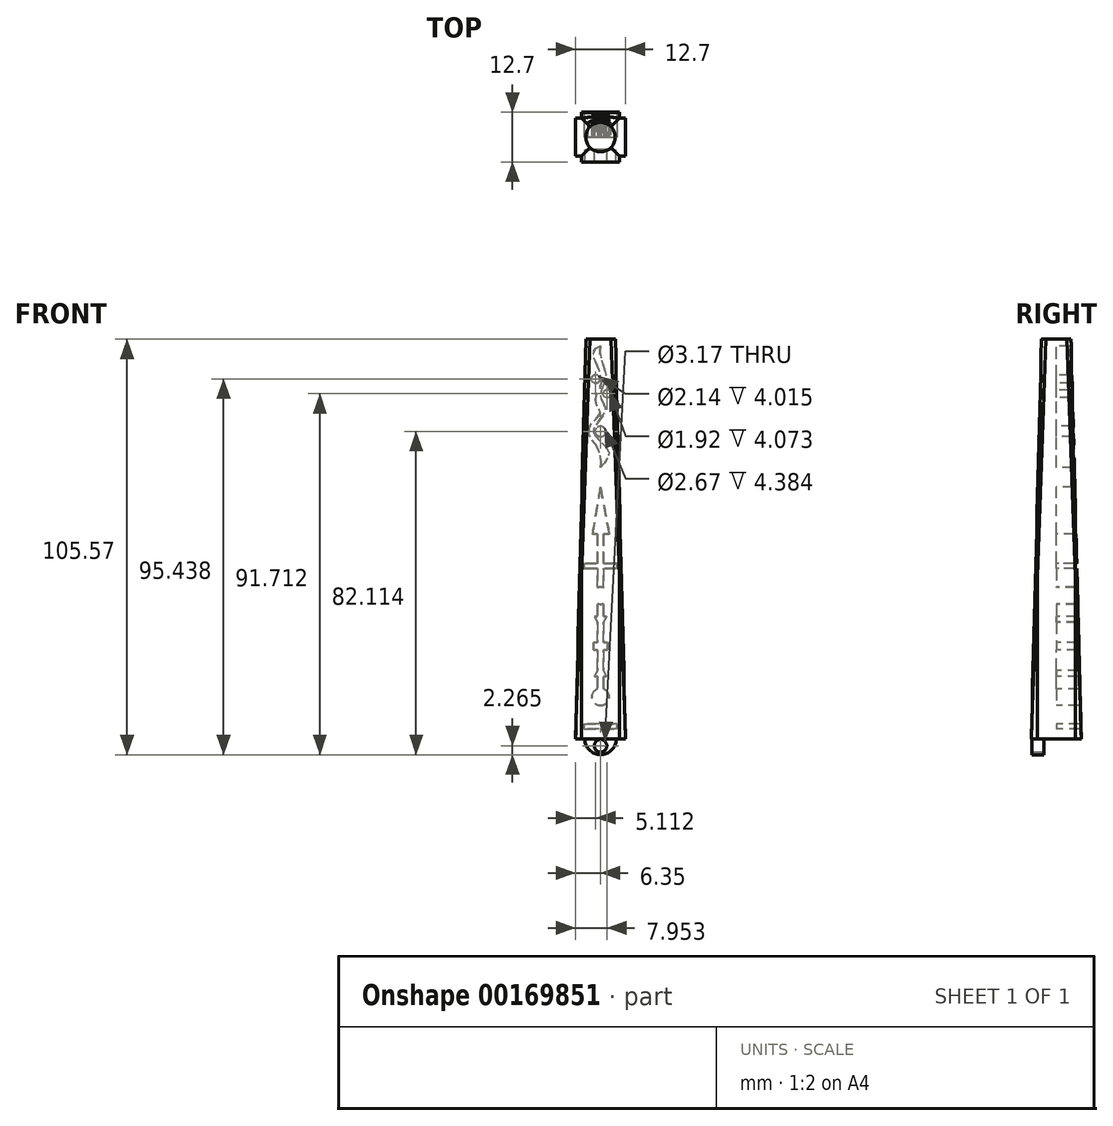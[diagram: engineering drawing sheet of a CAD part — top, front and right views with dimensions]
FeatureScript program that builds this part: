
annotation { "Feature Type Name" : "Feature", "Feature Type Description" : "" }
export const myFeature = defineFeature(function(context is Context, id is Id, definition is map)
    precondition{}
    {
        {
            var Q0;
            Q0=qCreatedBy(makeId("Top.planeOp"),FACE);
            var sketch = newSketch(context, id + "F0", { "sketchPlane" : qUnion([Q0])});
            skLineSegment(sketch, "E0.bottom", {"start": v(6.35, 6.35) * mm, "end": v(-6.35, 6.35) * mm});
            skLineSegment(sketch, "E0.top", {"start": v(6.35, -6.35) * mm, "end": v(-6.35, -6.35) * mm});
            skLineSegment(sketch, "E0.left", {"start": v(6.35, 6.35) * mm, "end": v(6.35, -6.35) * mm});
            skLineSegment(sketch, "E0.right", {"start": v(-6.35, 6.35) * mm, "end": v(-6.35, -6.35) * mm});
            skPoint(sketch, "E0.middle", {"position": v(0, 0) * mm});
            skSolve(sketch);
        }
        {
            var Q0;
            Q0=qCreatedBy(makeId("Top.planeOp"),FACE);
            cPlane(context, id + "F1", {"entities" : qUnion([Q0]), "cplaneType" : CPlaneType.OFFSET, "offset" : 101.6 * mm, "width" : 150 * mm, "height" : 150 * mm});
        }
        {
            var Q0;
            Q0=qCreatedBy(id+"F1.planeOp",FACE);
            var sketch = newSketch(context, id + "F2", { "sketchPlane" : qUnion([Q0])});
            skCircle(sketch, "E1", {"center": v(0, 0) * mm, "radius": 3.75 * mm});
            skSolve(sketch);
        }
        {
            var Q0;
            Q0=makeQuery(id+"F0.imprint","IMPRINT",FACE,{"disambiguationData":[TD([[makeQuery(id+"F0.imprint","IMPRINT",EDGE,{"derivedFrom":sQuery(id+"F0.wireOp",EDGE,"E0.bottom")}),1.0]])]});
            var Q1;
            Q1=makeQuery(id+"F2.imprint","IMPRINT",FACE,{"disambiguationData":[TD([[makeQuery(id+"F2.imprint","IMPRINT",EDGE,{"derivedFrom":sQuery(id+"F2.wireOp",EDGE,"E1")}),1.0]])]});
            loft(context, id + "F3", {"sheetProfilesArray" : [{ "sheetProfileEntities" : qUnion([Q0]) }, { "sheetProfileEntities" : qUnion([Q1]) }]});
        }
        {
            var Q0;
            Q0=qCreatedBy(makeId("Front.planeOp"),FACE);
            var sketch = newSketch(context, id + "F4", { "sketchPlane" : qUnion([Q0])});
            skCircle(sketch, "E2", {"center": v(0, 0) * mm, "radius": 3.97 * mm});
            skCircle(sketch, "E3", {"center": v(0, -1.7) * mm, "radius": 1.59 * mm});
            skSolve(sketch);
        }
        {
            var Q0;
            Q0=makeQuery(id+"F4.imprint","IMPRINT",FACE,{"disambiguationData":[TD([[makeQuery(id+"F4.imprint","IMPRINT",EDGE,{"derivedFrom":sQuery(id+"F4.wireOp",EDGE,"E2")}),1.0]])]});
            extrude(context, id + "F5", {"entities" : qUnion([Q0]), "operationType" : NewBodyOperationType.ADD, "depth" : 6.24 * mm});
        }
        {
            var Q0;
            Q0=makeQuery(id+"F5.opExtrude","CAP_FACE",FACE,{"disambiguationData":[OSD([sQuery(id+"F4.wireOp",EDGE,"E2"),sQuery(id+"F4.wireOp",EDGE,"E3")])],"isStart":true});
            extrude(context, id + "F6", {"entities" : qUnion([Q0]), "operationType" : NewBodyOperationType.REMOVE, "oppositeDirection" : true, "depth" : 3.17 * mm});
        }
        {
            var Q0;
            Q0=qCreatedBy(makeId("Front.planeOp"),FACE);
            var sketch = newSketch(context, id + "F7", { "sketchPlane" : qUnion([Q0])});
            skLineSegment(sketch, "E4.bottom", {"start": v(-4.19, 3.86) * mm, "end": v(4.19, 3.86) * mm});
            skLineSegment(sketch, "E4.top", {"start": v(-4.19, 2.51) * mm, "end": v(4.19, 2.51) * mm});
            skLineSegment(sketch, "E4.left", {"start": v(-4.19, 3.86) * mm, "end": v(-4.19, 2.51) * mm});
            skLineSegment(sketch, "E4.right", {"start": v(4.19, 3.86) * mm, "end": v(4.19, 2.51) * mm});
            skPoint(sketch, "E4.middle", {"position": v(0, 3.19) * mm});
            skLineSegment(sketch, "E5.bottom", {"start": v(-0.77, 3.86) * mm, "end": v(0.77, 3.86) * mm});
            skLineSegment(sketch, "E5.left", {"start": v(-0.77, 3.86) * mm, "end": v(-0.77, 8.5) * mm});
            skLineSegment(sketch, "E5.right", {"start": v(0.77, 3.86) * mm, "end": v(0.77, 8.5) * mm});
            skPoint(sketch, "E5.middle", {"position": v(0, 6.18) * mm});
            skPoint(sketch, "E5.middle.positionSnap0", {"position": v(0, 3.86) * mm});
            skPoint(sketch, "E5.centerSnap0", {"position": v(0, 3.86) * mm});
            skCircle(sketch, "E6", {"center": v(0, 10.7) * mm, "radius": 2.2 * mm});
            skLineSegment(sketch, "E7", {"start": v(0.77, 8.5) * mm, "end": v(0.77, 8.64) * mm});
            skLineSegment(sketch, "E8", {"start": v(-0.77, 8.5) * mm, "end": v(-0.77, 8.64) * mm});
            skPoint(sketch, "E9.orphan", {"position": v(0.77, 10.44) * mm});
            skPoint(sketch, "E10.orphan", {"position": v(-0.77, 10.44) * mm});
            skLineSegment(sketch, "E11.top", {"start": v(0.77, 15.97) * mm, "end": v(-0.77, 15.97) * mm});
            skLineSegment(sketch, "E11.left", {"start": v(0.77, 12.77) * mm, "end": v(0.77, 15.97) * mm});
            skLineSegment(sketch, "E11.right", {"start": v(-0.77, 12.77) * mm, "end": v(-0.77, 15.97) * mm});
            skLineSegment(sketch, "E12", {"start": v(0.77, 15.97) * mm, "end": v(1.54, 15.97) * mm});
            skLineSegment(sketch, "E13", {"start": v(1.54, 15.97) * mm, "end": v(-1.52, 15.97) * mm});
            skLineSegment(sketch, "E14", {"start": v(-1.52, 15.97) * mm, "end": v(0, 18.95) * mm});
            skLineSegment(sketch, "E15", {"start": v(0, 18.95) * mm, "end": v(1.54, 15.97) * mm});
            skLineSegment(sketch, "E16", {"start": v(0.77, 17.47) * mm, "end": v(0.77, 22.65) * mm});
            skLineSegment(sketch, "E17", {"start": v(-0.77, 17.45) * mm, "end": v(-0.77, 22.65) * mm});
            skLineSegment(sketch, "E18.top", {"start": v(1.77, 22.65) * mm, "end": v(0.77, 22.65) * mm});
            skLineSegment(sketch, "E18.left", {"start": v(1.77, 23.57) * mm, "end": v(1.77, 22.65) * mm});
            skLineSegment(sketch, "E18.right", {"start": v(-1.77, 23.57) * mm, "end": v(-1.77, 22.65) * mm});
            skPoint(sketch, "E18.middle", {"position": v(0, 23.11) * mm});
            skLineSegment(sketch, "E19.MirrorCS", {"start": v(-0.77, 29.7) * mm, "end": v(-0.77, 24.5) * mm});
            skLineSegment(sketch, "E20.MirrorCS", {"start": v(0.77, 29.68) * mm, "end": v(0.77, 24.5) * mm});
            skLineSegment(sketch, "E21.MirrorCS", {"start": v(1.77, 23.57) * mm, "end": v(1.77, 24.5) * mm});
            skLineSegment(sketch, "E22.MirrorCS", {"start": v(1.77, 24.5) * mm, "end": v(0.77, 24.5) * mm});
            skLineSegment(sketch, "E23.MirrorCS", {"start": v(-1.77, 23.57) * mm, "end": v(-1.77, 24.5) * mm});
            skLineSegment(sketch, "E24.MirrorCS", {"start": v(-1.52, 31.18) * mm, "end": v(0, 28.2) * mm});
            skLineSegment(sketch, "E25.MirrorCS", {"start": v(0, 28.2) * mm, "end": v(1.54, 31.18) * mm});
            skLineSegment(sketch, "E26.MirrorCS", {"start": v(0.77, 31.18) * mm, "end": v(-0.77, 31.18) * mm});
            skLineSegment(sketch, "E27.MirrorCS", {"start": v(1.54, 31.18) * mm, "end": v(-1.52, 31.18) * mm});
            skLineSegment(sketch, "E28.MirrorCS", {"start": v(0.77, 34.38) * mm, "end": v(0.77, 31.18) * mm});
            skLineSegment(sketch, "E29.MirrorCS", {"start": v(-0.77, 34.38) * mm, "end": v(-0.77, 31.18) * mm});
            skCircle(sketch, "E30.MirrorC", {"center": v(0, 36.44) * mm, "radius": 2.2 * mm});
            skLineSegment(sketch, "E31.MirrorCS", {"start": v(0.77, 43.29) * mm, "end": v(0.77, 38.64) * mm});
            skLineSegment(sketch, "E32.MirrorCS", {"start": v(-0.77, 43.29) * mm, "end": v(-0.77, 38.64) * mm});
            skLineSegment(sketch, "E33.MirrorCS", {"start": v(0.77, 38.64) * mm, "end": v(0.77, 38.5) * mm});
            skLineSegment(sketch, "E34.MirrorCS", {"start": v(-0.77, 38.64) * mm, "end": v(-0.77, 38.5) * mm});
            skLineSegment(sketch, "E35.MirrorCS", {"start": v(-4.19, 43.29) * mm, "end": v(4.19, 43.29) * mm});
            skLineSegment(sketch, "E36.MirrorCS", {"start": v(4.19, 43.29) * mm, "end": v(4.19, 44.63) * mm});
            skLineSegment(sketch, "E37.MirrorCS", {"start": v(-4.19, 44.63) * mm, "end": v(4.19, 44.63) * mm});
            skLineSegment(sketch, "E38.MirrorCS", {"start": v(-4.19, 43.29) * mm, "end": v(-4.19, 44.63) * mm});
            skPoint(sketch, "E39.MirrorCS.end.orphan", {"position": v(-0.77, 34.6) * mm});
            skPoint(sketch, "E39.MirrorCS.start.orphan", {"position": v(0.77, 34.6) * mm});
            skPoint(sketch, "E40.orphan", {"position": v(0.77, 24.04) * mm});
            skPoint(sketch, "E41.orphan", {"position": v(0.77, 23.11) * mm});
            skLineSegment(sketch, "E42.trimOffspring", {"start": v(-0.77, 22.65) * mm, "end": v(-1.77, 22.65) * mm});
            skPoint(sketch, "E43.orphan", {"position": v(-0.77, 23.11) * mm});
            skLineSegment(sketch, "E44.trimOffspring", {"start": v(-0.77, 24.5) * mm, "end": v(-1.77, 24.5) * mm});
            skPoint(sketch, "E45.orphan", {"position": v(0.77, 12.55) * mm});
            skLineSegment(sketch, "E46", {"start": v(0.77, 44.63) * mm, "end": v(0.77, 52.04) * mm});
            skLineSegment(sketch, "E47", {"start": v(-0.77, 44.63) * mm, "end": v(-0.77, 52.04) * mm});
            skLineSegment(sketch, "E48", {"start": v(0.77, 52.04) * mm, "end": v(2.25, 52.04) * mm});
            skLineSegment(sketch, "E49", {"start": v(2.25, 52.04) * mm, "end": v(0, 64.04) * mm});
            skLineSegment(sketch, "E50", {"start": v(0, 64.04) * mm, "end": v(-2.04, 52.04) * mm});
            skLineSegment(sketch, "E51", {"start": v(-2.04, 52.04) * mm, "end": v(-0.77, 52.04) * mm});
            skFitSpline(sketch, "E52", {"points": [v(0, 69) * mm, v(2.07, 73.14) * mm, v(-1.76, 78.24) * mm, v(1.22, 83.44) * mm, v(0, 87.26) * mm, v(1.32, 91.72) * mm, v(0, 97.25) * mm, v(0, 99.8) * mm], "startDerivative": vector(27.56, 29.2) * mm, "endDerivative": vector(3.44, 21.78) * mm});
            skFitSpline(sketch, "E53", {"points": [v(0, 69) * mm, v(0, 71.44) * mm, v(-1.54, 75.26) * mm, v(-3.03, 77.28) * mm, v(-2.29, 80.25) * mm, v(0, 82.8) * mm, v(-1.01, 84.82) * mm, v(-1.22, 86.95) * mm, v(0, 89.7) * mm, v(0, 92.36) * mm, v(-1.44, 96.3) * mm, v(-1.76, 98.73) * mm, v(0, 99.8) * mm], "startDerivative": vector(3.02, 28.92) * mm, "endDerivative": vector(31.24, 11.32) * mm});
            skCircle(sketch, "E54", {"center": v(-1.24, 91.47) * mm, "radius": 1.07 * mm});
            skCircle(sketch, "E55", {"center": v(1.6, 87.74) * mm, "radius": 0.96 * mm});
            skCircle(sketch, "E56", {"center": v(0, 78.14) * mm, "radius": 1.33 * mm});
            skSolve(sketch);
        }
        {
            var Q0;
            {var subQ2=sQuery(id+"F7.wireOp",EDGE,"E36.MirrorCS");Q0=makeQuery(id+"F7.imprint","IMPRINT",FACE,{"disambiguationData":[TD([[makeQuery(id+"F7.imprint","IMPRINT",EDGE,{"derivedFrom":subQ2}),1.0]])]});}
            var Q1;
            {var subQ2=sQuery(id+"F7.wireOp",EDGE,"E31.MirrorCS");Q1=makeQuery(id+"F7.imprint","IMPRINT",FACE,{"disambiguationData":[TD([[makeQuery(id+"F7.imprint","IMPRINT",EDGE,{"derivedFrom":subQ2}),-1.0]])]});}
            var Q2;
            {var subQ0=sQuery(id+"F7.wireOp",EDGE,"E30.MirrorC");var subQ1=makeQuery(id+"F7.imprint","INTERSECT",VERTEX,{"derivedFrom":[sQuery(id+"F7.wireOp",EDGE,"E28.MirrorCS"),subQ0]});Q2=makeQuery(id+"F7.imprint","IMPRINT",FACE,{"disambiguationData":[TD([[makeQuery(id+"F7.imprint","IMPRINT",EDGE,{"disambiguationData":[TD([[subQ1,-1.0]])],"derivedFrom":subQ0}),-1.0]])]});}
            var Q3;
            {var subQ0=sQuery(id+"F7.wireOp",EDGE,"E28.MirrorCS");Q3=makeQuery(id+"F7.imprint","IMPRINT",FACE,{"disambiguationData":[TD([[makeQuery(id+"F7.imprint","IMPRINT",EDGE,{"derivedFrom":subQ0}),-1.0]])]});}
            var Q4;
            {var subQ4=sQuery(id+"F7.wireOp",EDGE,"E24.MirrorCS");var subQ6=makeQuery(id+"F7.imprint","INTERSECT",VERTEX,{"derivedFrom":[sQuery(id+"F7.wireOp",EDGE,"E19.MirrorCS"),subQ4]});Q4=makeQuery(id+"F7.imprint","IMPRINT",FACE,{"disambiguationData":[TD([[makeQuery(id+"F7.imprint","IMPRINT",EDGE,{"disambiguationData":[TD([[subQ6,1.0]])],"derivedFrom":subQ4}),1.0]])]});}
            var Q5;
            {var subQ1=sQuery(id+"F7.wireOp",EDGE,"E16");Q5=makeQuery(id+"F7.imprint","IMPRINT",FACE,{"disambiguationData":[TD([[makeQuery(id+"F7.imprint","IMPRINT",EDGE,{"derivedFrom":subQ1}),1.0]])]});}
            var Q6;
            {var subQ1=sQuery(id+"F7.wireOp",EDGE,"E13");var subQ5=makeQuery(id+"F7.imprint","INTERSECT",VERTEX,{"derivedFrom":[sQuery(id+"F7.wireOp",EDGE,"E11.left"),subQ1]});Q6=makeQuery(id+"F7.imprint","IMPRINT",FACE,{"disambiguationData":[TD([[makeQuery(id+"F7.imprint","IMPRINT",EDGE,{"disambiguationData":[TD([[subQ5,1.0]])],"derivedFrom":subQ1}),-1.0]])]});}
            var Q7;
            {var subQ0=sQuery(id+"F7.wireOp",EDGE,"E11.left");Q7=makeQuery(id+"F7.imprint","IMPRINT",FACE,{"disambiguationData":[TD([[makeQuery(id+"F7.imprint","IMPRINT",EDGE,{"derivedFrom":subQ0}),1.0]])]});}
            var Q8;
            {var subQ0=sQuery(id+"F7.wireOp",EDGE,"E6");var subQ1=makeQuery(id+"F7.imprint","INTERSECT",VERTEX,{"derivedFrom":[subQ0,sQuery(id+"F7.wireOp",EDGE,"E11.left")]});Q8=makeQuery(id+"F7.imprint","IMPRINT",FACE,{"disambiguationData":[TD([[makeQuery(id+"F7.imprint","IMPRINT",EDGE,{"disambiguationData":[TD([[subQ1,-1.0]])],"derivedFrom":subQ0}),1.0]])]});}
            var Q9;
            Q9=makeQuery(id+"F7.imprint","IMPRINT",FACE,{"disambiguationData":[TD([[makeQuery(id+"F7.imprint","IMPRINT",EDGE,{"derivedFrom":sQuery(id+"F7.wireOp",EDGE,"E5.bottom")}),1.0]])]});
            var Q10;
            Q10=makeQuery(id+"F7.imprint","IMPRINT",FACE,{"disambiguationData":[TD([[makeQuery(id+"F7.imprint","IMPRINT",EDGE,{"derivedFrom":sQuery(id+"F7.wireOp",EDGE,"E4.top")}),1.0]])]});
            var Q11;
            {var subQ1=sQuery(id+"F7.wireOp",EDGE,"E46");Q11=makeQuery(id+"F7.imprint","IMPRINT",FACE,{"disambiguationData":[TD([[makeQuery(id+"F7.imprint","IMPRINT",EDGE,{"derivedFrom":subQ1}),1.0]])]});}
            var Q12;
            Q12=makeQuery(id+"F7.imprint","IMPRINT",FACE,{"disambiguationData":[TD([[makeQuery(id+"F7.imprint","IMPRINT",EDGE,{"derivedFrom":sQuery(id+"F7.wireOp",EDGE,"E52")}),1.0]])]});
            var Q13;
            Q13=makeQuery(id+"F7.imprint","IMPRINT",FACE,{"disambiguationData":[TD([[makeQuery(id+"F7.imprint","IMPRINT",EDGE,{"derivedFrom":sQuery(id+"F7.wireOp",EDGE,"E56")}),1.0]])]});
            var Q14;
            Q14=makeQuery(id+"F7.imprint","IMPRINT",FACE,{"disambiguationData":[TD([[makeQuery(id+"F7.imprint","IMPRINT",EDGE,{"derivedFrom":sQuery(id+"F7.wireOp",EDGE,"E55")}),1.0]])]});
            var Q15;
            Q15=makeQuery(id+"F7.imprint","IMPRINT",FACE,{"disambiguationData":[TD([[makeQuery(id+"F7.imprint","IMPRINT",EDGE,{"derivedFrom":sQuery(id+"F7.wireOp",EDGE,"E54")}),1.0]])]});
            extrude(context, id + "F8", {"entities" : qUnion([Q0, Q1, Q2, Q3, Q4, Q5, Q6, Q7, Q8, Q9, Q10, Q11, Q12, Q13, Q14, Q15]), "operationType" : NewBodyOperationType.REMOVE, "oppositeDirection" : true, "depth" : 25 * mm});
        }
        {
            var Q0;
            {var subQ0=makeQuery(id+"F0.imprint","IMPRINT",FACE,{"disambiguationData":[TD([[makeQuery(id+"F0.imprint","IMPRINT",EDGE,{"derivedFrom":sQuery(id+"F0.wireOp",EDGE,"E0.bottom")}),1.0]])]});Q0=makeQuery(id+"F6.boolean.opBoolean","MERGE",FACE,{"derivedFrom":[makeQuery(id+"F3.opLoft","CAP_FACE",FACE,{"disambiguationData":[OSD([subQ0])],"isStart":true}),makeQuery(id+"F6.opExtrude","SWEPT_FACE",FACE,{"disambiguationData":[OSD([subQ0,sQuery(id+"F4.wireOp",EDGE,"E2"),sQuery(id+"F4.wireOp",EDGE,"E3")])]})]});}
            var sketch = newSketch(context, id + "F9", { "sketchPlane" : qUnion([Q0])});
            skLineSegment(sketch, "E57.bottom", {"start": v(-6.35, 6.35) * mm, "end": v(-4.85, 6.35) * mm});
            skLineSegment(sketch, "E57.top", {"start": v(-6.35, 4.85) * mm, "end": v(-4.85, 4.85) * mm});
            skLineSegment(sketch, "E57.left", {"start": v(-6.35, 6.35) * mm, "end": v(-6.35, 4.85) * mm});
            skLineSegment(sketch, "E57.right", {"start": v(-4.85, 6.35) * mm, "end": v(-4.85, 4.85) * mm});
            skLineSegment(sketch, "E58.MirrorCS", {"start": v(4.85, 6.35) * mm, "end": v(4.85, 4.85) * mm});
            skLineSegment(sketch, "E59.MirrorCS", {"start": v(6.35, 6.35) * mm, "end": v(4.85, 6.35) * mm});
            skLineSegment(sketch, "E60.MirrorCS", {"start": v(6.35, 6.35) * mm, "end": v(6.35, 4.85) * mm});
            skLineSegment(sketch, "E61.MirrorCS", {"start": v(6.35, 4.85) * mm, "end": v(4.85, 4.85) * mm});
            skLineSegment(sketch, "E62.MirrorCS", {"start": v(-6.35, -6.35) * mm, "end": v(-4.85, -6.35) * mm});
            skLineSegment(sketch, "E63.MirrorCS", {"start": v(-4.85, -6.35) * mm, "end": v(-4.85, -4.85) * mm});
            skLineSegment(sketch, "E64.MirrorCS", {"start": v(-6.35, -4.85) * mm, "end": v(-4.85, -4.85) * mm});
            skLineSegment(sketch, "E65.MirrorCS", {"start": v(-6.35, -6.35) * mm, "end": v(-6.35, -4.85) * mm});
            skLineSegment(sketch, "E66.MirrorCS", {"start": v(6.35, -6.35) * mm, "end": v(4.85, -6.35) * mm});
            skLineSegment(sketch, "E67.MirrorCS", {"start": v(4.85, -6.35) * mm, "end": v(4.85, -4.85) * mm});
            skLineSegment(sketch, "E68.MirrorCS", {"start": v(6.35, -4.85) * mm, "end": v(4.85, -4.85) * mm});
            skLineSegment(sketch, "E69.MirrorCS", {"start": v(6.35, -6.35) * mm, "end": v(6.35, -4.85) * mm});
            skSolve(sketch);
        }
        {
            var Q0;
            Q0=makeQuery(id+"F9.imprint","IMPRINT",FACE,{"disambiguationData":[TD([[makeQuery(id+"F9.imprint","IMPRINT",EDGE,{"derivedFrom":sQuery(id+"F9.wireOp",EDGE,"E58.MirrorCS")}),1.0]])]});
            var Q1;
            Q1=makeQuery(id+"F9.imprint","IMPRINT",FACE,{"disambiguationData":[TD([[makeQuery(id+"F9.imprint","IMPRINT",EDGE,{"derivedFrom":sQuery(id+"F9.wireOp",EDGE,"E57.bottom")}),-1.0]])]});
            var Q2;
            Q2=makeQuery(id+"F9.imprint","IMPRINT",FACE,{"disambiguationData":[TD([[makeQuery(id+"F9.imprint","IMPRINT",EDGE,{"derivedFrom":sQuery(id+"F9.wireOp",EDGE,"E62.MirrorCS")}),-1.0]])]});
            var Q3;
            Q3=makeQuery(id+"F9.imprint","IMPRINT",FACE,{"disambiguationData":[TD([[makeQuery(id+"F9.imprint","IMPRINT",EDGE,{"derivedFrom":sQuery(id+"F9.wireOp",EDGE,"E66.MirrorCS")}),-1.0]])]});
            extrude(context, id + "F10", {"entities" : qUnion([Q0, Q1, Q2, Q3]), "operationType" : NewBodyOperationType.REMOVE, "oppositeDirection" : true, "depth" : 200 * mm});
        }
    });
